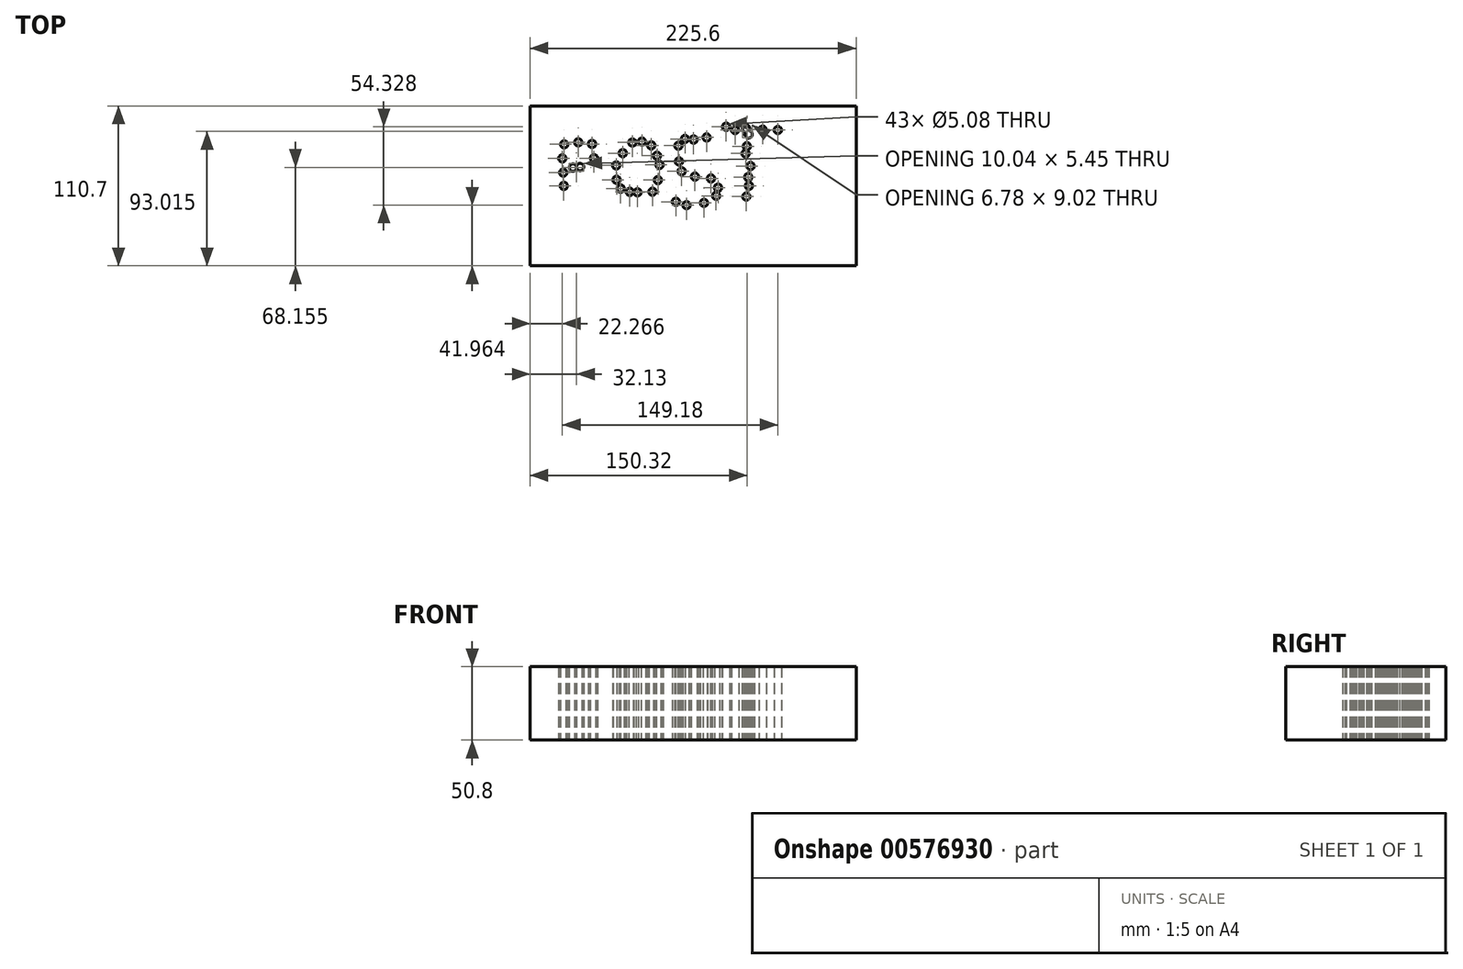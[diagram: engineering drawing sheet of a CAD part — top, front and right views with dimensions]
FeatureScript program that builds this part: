
annotation { "Feature Type Name" : "Feature", "Feature Type Description" : "" }
export const myFeature = defineFeature(function(context is Context, id is Id, definition is map)
    precondition{}
    {
        {
            var Q0;
            Q0=qCreatedBy(makeId("Top.planeOp"),FACE);
            var sketch = newSketch(context, id + "F0", { "sketchPlane" : qUnion([Q0])});
            skLineSegment(sketch, "E0.bottom", {"start": v(112.8, 55.35) * mm, "end": v(-112.8, 55.35) * mm});
            skLineSegment(sketch, "E0.top", {"start": v(112.8, -55.35) * mm, "end": v(-112.8, -55.35) * mm});
            skLineSegment(sketch, "E0.left", {"start": v(112.8, 55.35) * mm, "end": v(112.8, -55.35) * mm});
            skLineSegment(sketch, "E0.right", {"start": v(-112.8, 55.35) * mm, "end": v(-112.8, -55.35) * mm});
            skPoint(sketch, "E0.middle", {"position": v(0, 0) * mm});
            skSolve(sketch);
        }
        {
            var Q0;
            Q0=makeQuery(id+"F0.imprint","IMPRINT",FACE,{"disambiguationData":[TD([[makeQuery(id+"F0.imprint","IMPRINT",EDGE,{"derivedFrom":sQuery(id+"F0.wireOp",EDGE,"E0.bottom")}),1.0]])]});
            extrude(context, id + "F1", {"entities" : qUnion([Q0]), "depth" : 25.4 * mm, "offsetDistance" : 25.4 * mm});
        }
        {
            var Q0;
            Q0=qCreatedBy(makeId("Top.planeOp"),FACE);
            var sketch = newSketch(context, id + "F2", { "sketchPlane" : qUnion([Q0])});
            skPoint(sketch, "E1", {"position": v(-89.2, 28.7) * mm});
            skPoint(sketch, "E2", {"position": v(-90.53, 19) * mm});
            skPoint(sketch, "E3", {"position": v(-89.87, 9.15) * mm});
            skPoint(sketch, "E4", {"position": v(-89.48, 0) * mm});
            skPoint(sketch, "E5", {"position": v(-79.5, 30.1) * mm});
            skPoint(sketch, "E6", {"position": v(-69.93, 29) * mm});
            skPoint(sketch, "E7", {"position": v(-68.6, 19.16) * mm});
            skPoint(sketch, "E8", {"position": v(-78.18, 13) * mm});
            skPoint(sketch, "E9", {"position": v(-83.15, 12.62) * mm});
            skPoint(sketch, "E10", {"position": v(-42.04, 29.98) * mm});
            skPoint(sketch, "E11", {"position": v(-48.7, 22.61) * mm});
            skPoint(sketch, "E12", {"position": v(-53.19, 14.11) * mm});
            skPoint(sketch, "E13", {"position": v(-52.96, 4.13) * mm});
            skPoint(sketch, "E14", {"position": v(-50.14, -1.96) * mm});
            skPoint(sketch, "E15", {"position": v(-43.84, -4.15) * mm});
            skPoint(sketch, "E16", {"position": v(-38.5, -4.52) * mm});
            skPoint(sketch, "E17", {"position": v(-28.1, -4.08) * mm});
            skPoint(sketch, "E18", {"position": v(-24.36, 3.96) * mm});
            skPoint(sketch, "E19", {"position": v(-23.18, 14.52) * mm});
            skPoint(sketch, "E20", {"position": v(-25.01, 20.87) * mm});
            skPoint(sketch, "E21", {"position": v(-28.99, 28.01) * mm});
            skPoint(sketch, "E22", {"position": v(-35.42, 30.63) * mm});
            skPoint(sketch, "E23", {"position": v(9.38, 33.5) * mm});
            skPoint(sketch, "E24", {"position": v(0.35, 32.03) * mm});
            skPoint(sketch, "E25", {"position": v(-5.61, 32.43) * mm});
            skPoint(sketch, "E26", {"position": v(-10.14, 27.78) * mm});
            skPoint(sketch, "E27", {"position": v(-9.77, 16.86) * mm});
            skPoint(sketch, "E28", {"position": v(-7.88, 10.03) * mm});
            skPoint(sketch, "E29", {"position": v(1.26, 6.4) * mm});
            skPoint(sketch, "E30", {"position": v(12.35, 5.09) * mm});
            skPoint(sketch, "E31", {"position": v(17.25, -1.3) * mm});
            skPoint(sketch, "E32", {"position": v(15.92, -6.92) * mm});
            skPoint(sketch, "E33", {"position": v(7.53, -11.82) * mm});
            skPoint(sketch, "E34", {"position": v(-4.53, -13.39) * mm});
            skPoint(sketch, "E35", {"position": v(-11.92, -11) * mm});
            skPoint(sketch, "E36", {"position": v(22.88, 40.94) * mm});
            skPoint(sketch, "E37", {"position": v(29.05, 38.64) * mm});
            skPoint(sketch, "E38", {"position": v(36.64, 39.72) * mm});
            skPoint(sketch, "E39", {"position": v(48.08, 38.9) * mm});
            skPoint(sketch, "E40", {"position": v(58.65, 38.63) * mm});
            skPoint(sketch, "E41", {"position": v(38.4, 35.61) * mm});
            skSolve(sketch);
        }
        {
            var Q0;
            Q0=qCreatedBy(makeId("Top.planeOp"),FACE);
            var sketch = newSketch(context, id + "F3", { "sketchPlane" : qUnion([Q0])});
            skPoint(sketch, "E42", {"position": v(37.2, 27.38) * mm});
            skPoint(sketch, "E43", {"position": v(39.75, 13.68) * mm});
            skPoint(sketch, "E44", {"position": v(38.64, 0) * mm});
            skPoint(sketch, "E45", {"position": v(36.33, 22.36) * mm});
            skPoint(sketch, "E46", {"position": v(38.15, 6.03) * mm});
            skPoint(sketch, "E47", {"position": v(36.81, -7.44) * mm});
            skSolve(sketch);
        }
        {
            var Q0;
            Q0=sQuery(id+"F2.wireOp",VERTEX,"E1");
            var Q1;
            Q1=sQuery(id+"F2.wireOp",VERTEX,"E5");
            var Q2;
            Q2=sQuery(id+"F2.wireOp",VERTEX,"E6");
            var Q3;
            Q3=sQuery(id+"F2.wireOp",VERTEX,"E7");
            var Q4;
            Q4=sQuery(id+"F2.wireOp",VERTEX,"E8");
            var Q5;
            Q5=sQuery(id+"F2.wireOp",VERTEX,"E9");
            var Q6;
            Q6=sQuery(id+"F2.wireOp",VERTEX,"E2");
            var Q7;
            Q7=sQuery(id+"F2.wireOp",VERTEX,"E3");
            var Q8;
            Q8=sQuery(id+"F2.wireOp",VERTEX,"E4");
            var Q9;
            Q9=sQuery(id+"F2.wireOp",VERTEX,"E22");
            var Q10;
            Q10=sQuery(id+"F2.wireOp",VERTEX,"E10");
            var Q11;
            Q11=sQuery(id+"F2.wireOp",VERTEX,"E11");
            var Q12;
            Q12=sQuery(id+"F2.wireOp",VERTEX,"E12");
            var Q13;
            Q13=sQuery(id+"F2.wireOp",VERTEX,"E13");
            var Q14;
            Q14=sQuery(id+"F2.wireOp",VERTEX,"E14");
            var Q15;
            Q15=sQuery(id+"F2.wireOp",VERTEX,"E17");
            var Q16;
            Q16=sQuery(id+"F2.wireOp",VERTEX,"E18");
            var Q17;
            Q17=sQuery(id+"F2.wireOp",VERTEX,"E16");
            var Q18;
            Q18=sQuery(id+"F2.wireOp",VERTEX,"E15");
            var Q19;
            Q19=sQuery(id+"F2.wireOp",VERTEX,"E29");
            var Q20;
            Q20=sQuery(id+"F2.wireOp",VERTEX,"E35");
            var Q21;
            Q21=sQuery(id+"F2.wireOp",VERTEX,"E34");
            var Q22;
            Q22=sQuery(id+"F2.wireOp",VERTEX,"E33");
            var Q23;
            Q23=sQuery(id+"F3.wireOp",VERTEX,"E47");
            var Q24;
            Q24=sQuery(id+"F3.wireOp",VERTEX,"E44");
            var Q25;
            Q25=sQuery(id+"F2.wireOp",VERTEX,"E31");
            var Q26;
            Q26=sQuery(id+"F2.wireOp",VERTEX,"E32");
            var Q27;
            Q27=sQuery(id+"F2.wireOp",VERTEX,"E30");
            var Q28;
            Q28=sQuery(id+"F2.wireOp",VERTEX,"E28");
            var Q29;
            Q29=sQuery(id+"F2.wireOp",VERTEX,"E19");
            var Q30;
            Q30=sQuery(id+"F2.wireOp",VERTEX,"E21");
            var Q31;
            Q31=sQuery(id+"F2.wireOp",VERTEX,"E20");
            var Q32;
            Q32=sQuery(id+"F2.wireOp",VERTEX,"E27");
            var Q33;
            Q33=sQuery(id+"F2.wireOp",VERTEX,"E26");
            var Q34;
            Q34=sQuery(id+"F2.wireOp",VERTEX,"E36");
            var Q35;
            Q35=sQuery(id+"F2.wireOp",VERTEX,"E37");
            var Q36;
            Q36=sQuery(id+"F2.wireOp",VERTEX,"E38");
            var Q37;
            Q37=sQuery(id+"F2.wireOp",VERTEX,"E39");
            var Q38;
            Q38=sQuery(id+"F2.wireOp",VERTEX,"E40");
            var Q39;
            Q39=sQuery(id+"F2.wireOp",VERTEX,"E23");
            var Q40;
            Q40=sQuery(id+"F2.wireOp",VERTEX,"E24");
            var Q41;
            Q41=sQuery(id+"F2.wireOp",VERTEX,"E25");
            var Q42;
            Q42=sQuery(id+"F3.wireOp",VERTEX,"E46");
            var Q43;
            Q43=sQuery(id+"F3.wireOp",VERTEX,"E43");
            var Q44;
            Q44=sQuery(id+"F3.wireOp",VERTEX,"E45");
            var Q45;
            Q45=sQuery(id+"F2.wireOp",VERTEX,"E41");
            var Q46;
            Q46=sQuery(id+"F3.wireOp",VERTEX,"E42");
            var Q47;
            Q47=makeQuery(id+"F1.opExtrude","SWEPT_BODY",BODY,{"disambiguationData":[OSD([sQuery(id+"F0.wireOp",EDGE,"E0.bottom"),sQuery(id+"F0.wireOp",EDGE,"E0.top"),sQuery(id+"F0.wireOp",EDGE,"E0.left"),sQuery(id+"F0.wireOp",EDGE,"E0.right")])]});
            hole(context, id + "F4", {"style" : HoleStyle.SIMPLE, "endStyle" : HoleEndStyle.THROUGH, "oppositeDirection" : true, "holeDiameter" : 5.08 * mm, "isTappedThrough" : true, "tappedDepth" : 12.7 * mm, "tapClearance" : 3, "locations" : qUnion([Q0, Q1, Q2, Q3, Q4, Q5, Q6, Q7, Q8, Q9, Q10, Q11, Q12, Q13, Q14, Q15, Q16, Q17, Q18, Q19, Q20, Q21, Q22, Q23, Q24, Q25, Q26, Q27, Q28, Q29, Q30, Q31, Q32, Q33, Q34, Q35, Q36, Q37, Q38, Q39, Q40, Q41, Q42, Q43, Q44, Q45, Q46]), "scope" : qUnion([Q47])});
        }
        {
            var Q0;
            Q0=makeQuery(id+"F1.opExtrude","SWEPT_BODY",BODY,{"disambiguationData":[OSD([sQuery(id+"F0.wireOp",EDGE,"E0.bottom"),sQuery(id+"F0.wireOp",EDGE,"E0.top"),sQuery(id+"F0.wireOp",EDGE,"E0.left"),sQuery(id+"F0.wireOp",EDGE,"E0.right")])]});
            var Q1;
            Q1=qCreatedBy(makeId("Top.planeOp"),FACE);
            mirror(context, id + "F5", {"operationType" : NewBodyOperationType.ADD, "entities" : qUnion([Q0]), "mirrorPlane" : qUnion([Q1])});
        }
    });
